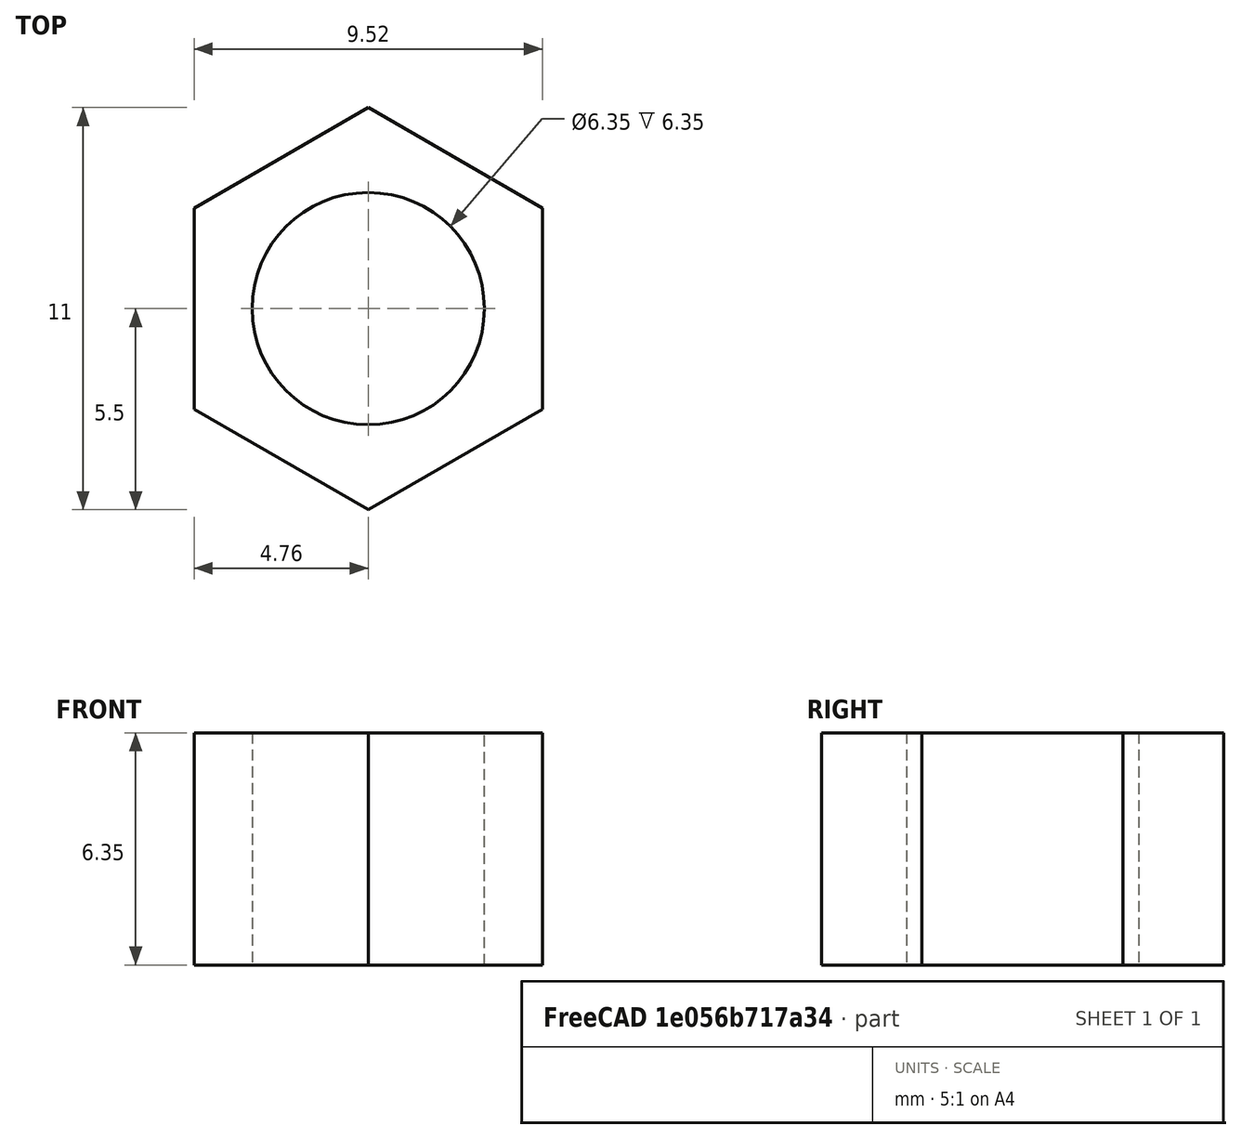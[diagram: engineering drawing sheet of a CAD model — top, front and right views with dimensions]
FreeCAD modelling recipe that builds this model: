
FCSTD DOCUMENT  (FreeCAD 0.19R24291 (Git))
Label: NutHex0.25-20
License: All rights reserved
LicenseURL: http://en.wikipedia.org/wiki/All_rights_reserved
objects: Sketcher::SketchObject×1, PartDesign::Pad×1, PartDesign::Body×1
note: 4 computed .brp shape members not serialized (recipe doc carries the construction recipe); baked Part::Feature solids carry a one-line shape summary decoded from their .brp

FEATURE [Sketcher::SketchObject] Sketch
  FullyConstrained = true
  MapMode = 5
  Support = -> [XY_Plane]
  sketch-geometry (8):
    g0: LineSegment StartX=4.7625 StartY=-2.74963 StartZ=0 EndX=4.7625 EndY=2.74963 EndZ=0
    g1: LineSegment StartX=4.7625 StartY=2.74963 StartZ=0 EndX=-9e-16 EndY=5.49926 EndZ=0
    g2: LineSegment StartX=-9e-16 StartY=5.49926 StartZ=0 EndX=-4.7625 EndY=2.74963 EndZ=0
    g3: LineSegment StartX=-4.7625 StartY=2.74963 StartZ=0 EndX=-4.7625 EndY=-2.74963 EndZ=0
    g4: LineSegment StartX=-4.7625 StartY=-2.74963 StartZ=0 EndX=0 EndY=-5.49926 EndZ=0
    g5: LineSegment StartX=0 StartY=-5.49926 StartZ=0 EndX=4.7625 EndY=-2.74963 EndZ=0
    g6: Circle CenterX=0 CenterY=0 CenterZ=0 NormalX=0 NormalY=0 NormalZ=1 AngleXU=0 Radius=5.49926
    g7: Circle CenterX=0 CenterY=0 CenterZ=0 NormalX=0 NormalY=0 NormalZ=1 AngleXU=0 Radius=3.175
  constraints (18):
    c: Coincident(g0,g1)
    c: Coincident(g1,g2)
    c: Coincident(g2,g3)
    c: Coincident(g3,g4)
    c: Coincident(g4,g5)
    c: Coincident(g5,g0)
    c: Equal(g0, g1-g5) x5
    c: PointOnObject(g0,g6)
    c: PointOnObject(g1,g6)
    c: PointOnObject(g2,g6)
    c: PointOnObject(g3,g6)
    c: PointOnObject(g4,g6)
    c: PointOnObject(g5,g6)
    c: Coincident(g6,g-1)
    c: Vertical(g3)
    c: DistanceX(g2,g0) = 9.525
    c: Diameter(g7) = 6.35
    c: Coincident(g7,g-1)
FEATURE [PartDesign::Pad] Pad
  Direction = (1,1,1)
  Length = 6.35
  Length2 = 99.9998
  Profile = -> Sketch
  Type = 0
FEATURE [PartDesign::Body] Body
  Group = -> [Sketch,Pad]
  Origin = -> Origin
  Tip = -> Pad
